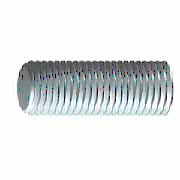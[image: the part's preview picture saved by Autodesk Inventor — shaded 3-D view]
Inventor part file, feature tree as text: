
AUTODESK INVENTOR PART (.ipt)
format: ipt  version: 2018 (Build 220112000, 112)  size: 126,464 bytes
history: native  units: mm
features: revolve x1, sketch x1
ambient origin geometry x8: Origin, YZ Plane, XZ Plane, XY Plane, X Axis, Y Axis, Z Axis, Center Point
bodies: Solid1 (feature_tree)
feature tree (2):
  revolve  "Revolution 1"  [1 undecoded]
  sketch  "Sketch 1"  dims[d2=90.0deg d3=10.0mm d4=0.0mm d5=0.0mm d6=0.0mm d7=0.0mm]
note: 1 required parameter value undecoded (feature->parameter linkage not recoverable at this tier; creation-order binding heuristic only, values carry confidence <= 0.55)
